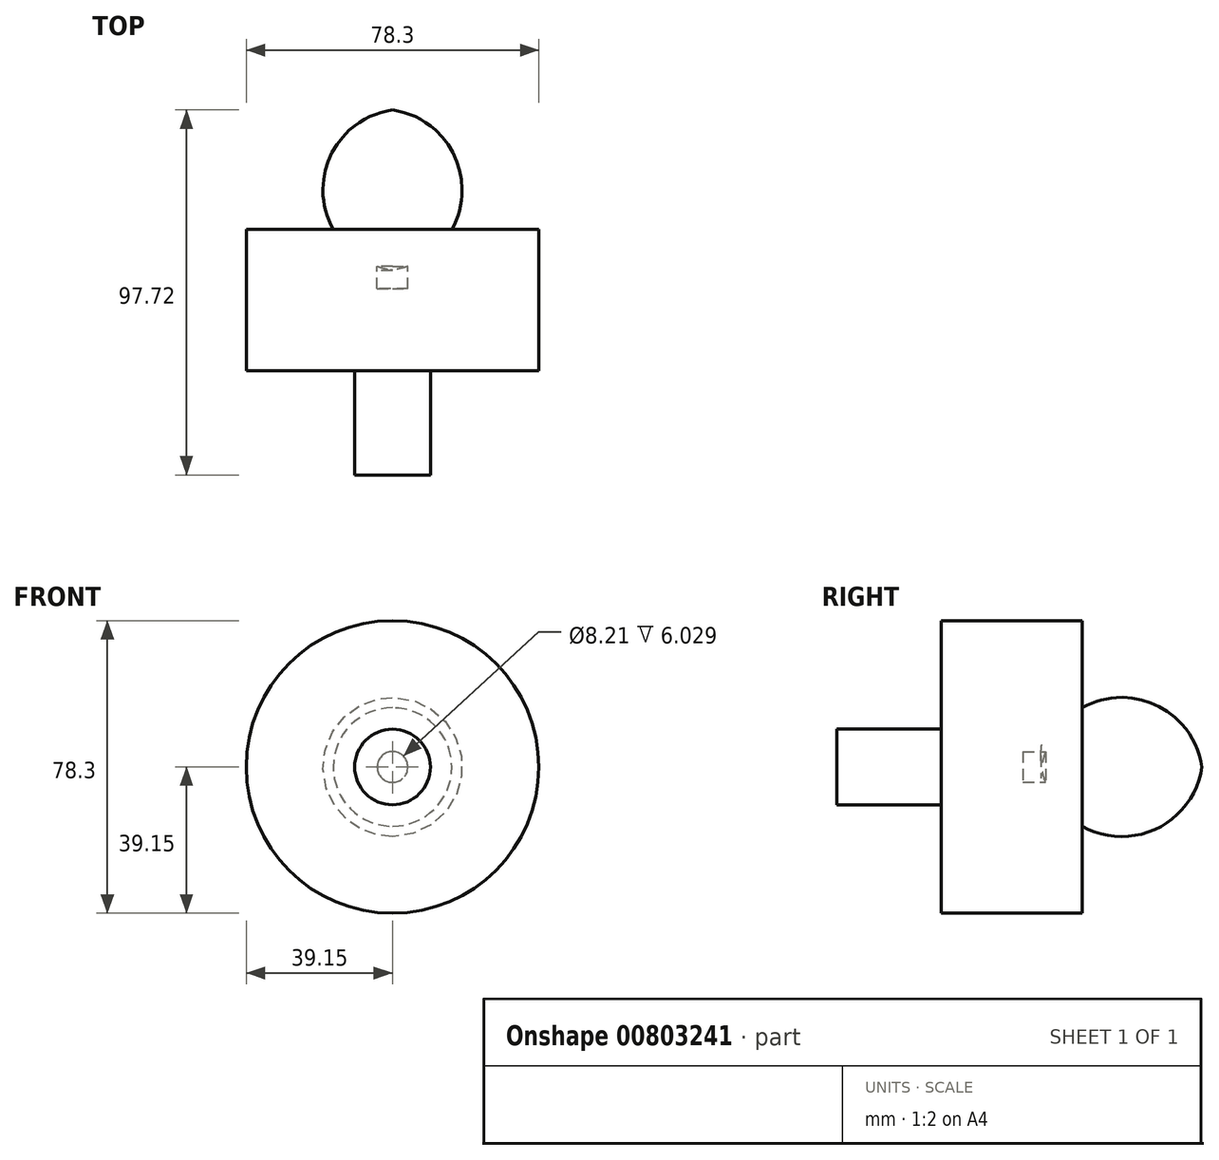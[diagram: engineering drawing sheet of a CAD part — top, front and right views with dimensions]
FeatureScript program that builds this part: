
annotation { "Feature Type Name" : "Feature", "Feature Type Description" : "" }
export const myFeature = defineFeature(function(context is Context, id is Id, definition is map)
    precondition{}
    {
        {
            var Q0;
            Q0=qCreatedBy(makeId("Top.planeOp"),FACE);
            var sketch = newSketch(context, id + "F0", { "sketchPlane" : qUnion([Q0])});
            skLineSegment(sketch, "E0", {"start": v(0, 75.2) * mm, "end": v(0, -75.2) * mm, "construction": true});
            skLineSegment(sketch, "E1.bottom", {"start": v(0, 14.97) * mm, "end": v(4.1, 14.97) * mm});
            skLineSegment(sketch, "E1.top", {"start": v(0, -34.86) * mm, "end": v(10.13, -34.86) * mm});
            skLineSegment(sketch, "E1.right", {"start": v(10.13, -6.94) * mm, "end": v(10.13, -34.86) * mm});
            skLineSegment(sketch, "E2.bottom", {"start": v(15.86, 30.84) * mm, "end": v(39.15, 30.84) * mm});
            skLineSegment(sketch, "E2.top", {"start": v(10.13, -6.94) * mm, "end": v(39.15, -6.94) * mm});
            skLineSegment(sketch, "E2.left", {"start": v(4.1, 21) * mm, "end": v(4.1, 14.97) * mm});
            skLineSegment(sketch, "E2.right", {"start": v(39.15, 30.84) * mm, "end": v(39.15, -6.94) * mm});
            skArc(sketch, "E3", {"start": v(0, 20) * mm, "mid": v(2.08, 20.4) * mm, "end": v(4.1, 21) * mm});
            skArc(sketch, "E4.trimOffspring", {"start": v(15.86, 30.84) * mm, "mid": v(16.38, 51.03) * mm, "end": v(0, 62.86) * mm});
            skLineSegment(sketch, "E5", {"start": v(0, 62.86) * mm, "end": v(0, -34.86) * mm});
            skSolve(sketch);
        }
        {
            var Q0;
            {var subQ3=sQuery(id+"F0.wireOp",EDGE,"E1.bottom");Q0=makeQuery(id+"F0.imprint","IMPRINT",FACE,{"disambiguationData":[TD([[makeQuery(id+"F0.imprint","IMPRINT",EDGE,{"derivedFrom":subQ3}),-1.0]])]});}
            var Q1;
            Q1=sQuery(id+"F0.wireOp",EDGE,"E5");
            revolve(context, id + "F1", {"surfaceOperationType" : NewSurfaceOperationType.NEW, "entities" : qUnion([Q0]), "axis" : qUnion([Q1]), "revolveType" : RevolveType.FULL});
        }
    });
